# Revit family: QF_ELECTROLUXPROFESSIONAL_1LSNST_TD6-37_S
name_source: partatom
category: Attrezzature speciali
units: mm (PartAtom-declared; Revit-internal decimal feet)

## family parameters
Basato su piano di lavoro = No
Condiviso = No
Punto di calcolo locali = No
Quota connettore circolare = Usa diametro
Sempre verticale = Sì
Taglio con vuoti quando caricato = No
Tipo di parte = Normale

## types (14) — shared parameters
Depth Actual = 1640 mm  [stored 5.38058 ft]
Height Actual = 1855 mm  [stored 6.08596 ft]
Latent Heat Output = 0.0
Length Actual = 960 mm  [stored 3.14961 ft]
Modello = TD6-37
Produttore = Electrolux Professional
Sensible Heat Output = 0.0
URL = www.electroluxprofessional.com
Weight = 337
zero-valued in all types: Gas KW, Prospetto di default, Steam Pounds per Hour

## per-type parameters (varying)
| type | Cycle | Descrizione | Item Number | Phase | Volts | Watts |
| 9873030084 | 60 Hz | TUMBLE DRYER TD6-37 MARINE 37KG GALVA.DRUM STEAM 46KW 440/60/3 COMPASS PRO 6G81 SLVR/SLVR DO.RIGHT REV MB STOP DISCO... | 1L0GWK | 3 | 440 V | 1500 W |
| 9873030079 | 50 Hz | TUMBLE DRYER TD6-37 37KG SST DRUM STEAM 46KW 380-415/50/3 COMPASS PRO 6G81 SST/SST DO.LEFT REV MB STOP DISCON DMPR | 1LA23B | 3 | 415 V | 1500 W |
| 9873030062 | 60 Hz | TUMBLE DRYER TD6-37 MARINE 37KG SST DRUM STEAM 46KW 208-240/60/1 COMPASS PRO 6G81 SLVR/SLVR DO.RIGHT REV MB STOP DIS... | 1LSPBU | 1 | 240 V | 1700 W |
| 9873030085 | 50 Hz | TUMBLE DRYER TD6-37 37KG GALVA.DRUM STEAM 46KW 380-415/50/3N COMPASS PRO 6G81 SLVR/SLVR DO.RIGHT REV MB STOP DISCON ... | 1L0GWL | 3 | 415 V | 1500 W |
| 9873030090 | 50 Hz | TUMBLE DRYER TD6-37 37KG SST DRUM STEAM 46KW 380-415/50/3 COMPASS PRO 6G81 SLVR/SLVR DO.RIGHT REV MB STOP DISCON DMPR | 1L0GXA | 3 | 415 V | 1500 W |
| 9873030116 | 50 Hz | TUMBLE DRYER TD6-37 37KG GALVA.DRUM STEAM 46KW 380-415/50/3N COMPASS PRO 6G82 SLVR/SLVR DO.RIGHT REV STOP DISCON DMPR | 1LT69G | 3 | 415 V | 1500 W |
| 9873030010 | 50 Hz | TUMBLE DRYER TD6-37 37KG SST DRUM STEAM 46KW 380-415/50/3N COMPASS PRO 6G81 SLVR/SLVR DO.RIGHT REV MB STOP DISCON DMPR | 1L0G64 | 3 | 415 V | 1500 W |
| 9873030103 | 60 Hz | TUMBLE DRYER TD6-37 37KG GALVA.DRUM STEAM 46KW 208-240/60/3 COMPASS PRO 6G82 SLVR/SLVR DO.LEFT REV DISCON DMPR | 1L0H4G | 3 | 240 V | 1500 W |
| 9873030060 | 50 Hz | TUMBLE DRYER TD6-37 37KG GALVA.DRUM STEAM 46KW 230/50/1 COMPASS PRO 6G81 SLVR/SLVR DO.RIGHT REV MB DISCON DMPR | 1LSPBM | 1 | 230 V | 1700 W |
| 9873030105 | 60 Hz | TUMBLE DRYER TD6-37 37KG SST DRUM STEAM 46KW 200/60/3 COMPASS PRO 6G86 SLVR/SLVR DO.RIGHT REV DISCON DMPR | 1L0H7Z | 3 | 200 V | 1500 W |
| 9873030016 | 50 Hz | TUMBLE DRYER TD6-37 37KG GALVA.DRUM STEAM 46KW 380-415/50/3N COMPASS PRO 6G82 SLVR/SLVR DO.RIGHT REV STOP DISCON DMPR | 1L0G6A | 3 | 415 V | 1500 W |
| 9873030018 | 50 Hz | TUMBLE DRYER TD6-37 37KG SST DRUM STEAM 46KW 380-415/50/3N COMPASS PRO 6G82 SLVR/SLVR DO.RIGHT REV STOP DISCON DMPR | 1L0G6C | 3 | 415 V | 1500 W |
| 9873030046 | 50 Hz | TUMBLE DRYER TD6-37 37KG SST DRUM STEAM 46KW 380-415/50/3N COMPASS PRO 6G82 SST/SST DO.RIGHT REV DISCON DMPR | 1L0GCM | 3 | 415 V | 1500 W |
| 9873030104 | 50 Hz | TUMBLE DRYER TD6-37 37KG SST DRUM STEAM 46KW 200/50/3 COMPASS PRO 6G86 SLVR/SLVR DO.RIGHT REV DISCON DMPR | 1L0H7Y | 3 | 200 V | 1500 W |

note: [stored X ft] marks values corroborated as IEEE doubles in the binary element streams (Revit-internal decimal feet)

## geometry (parser evidence)
native form markers: Blend x8
no freeform markers — native parametric forms only
